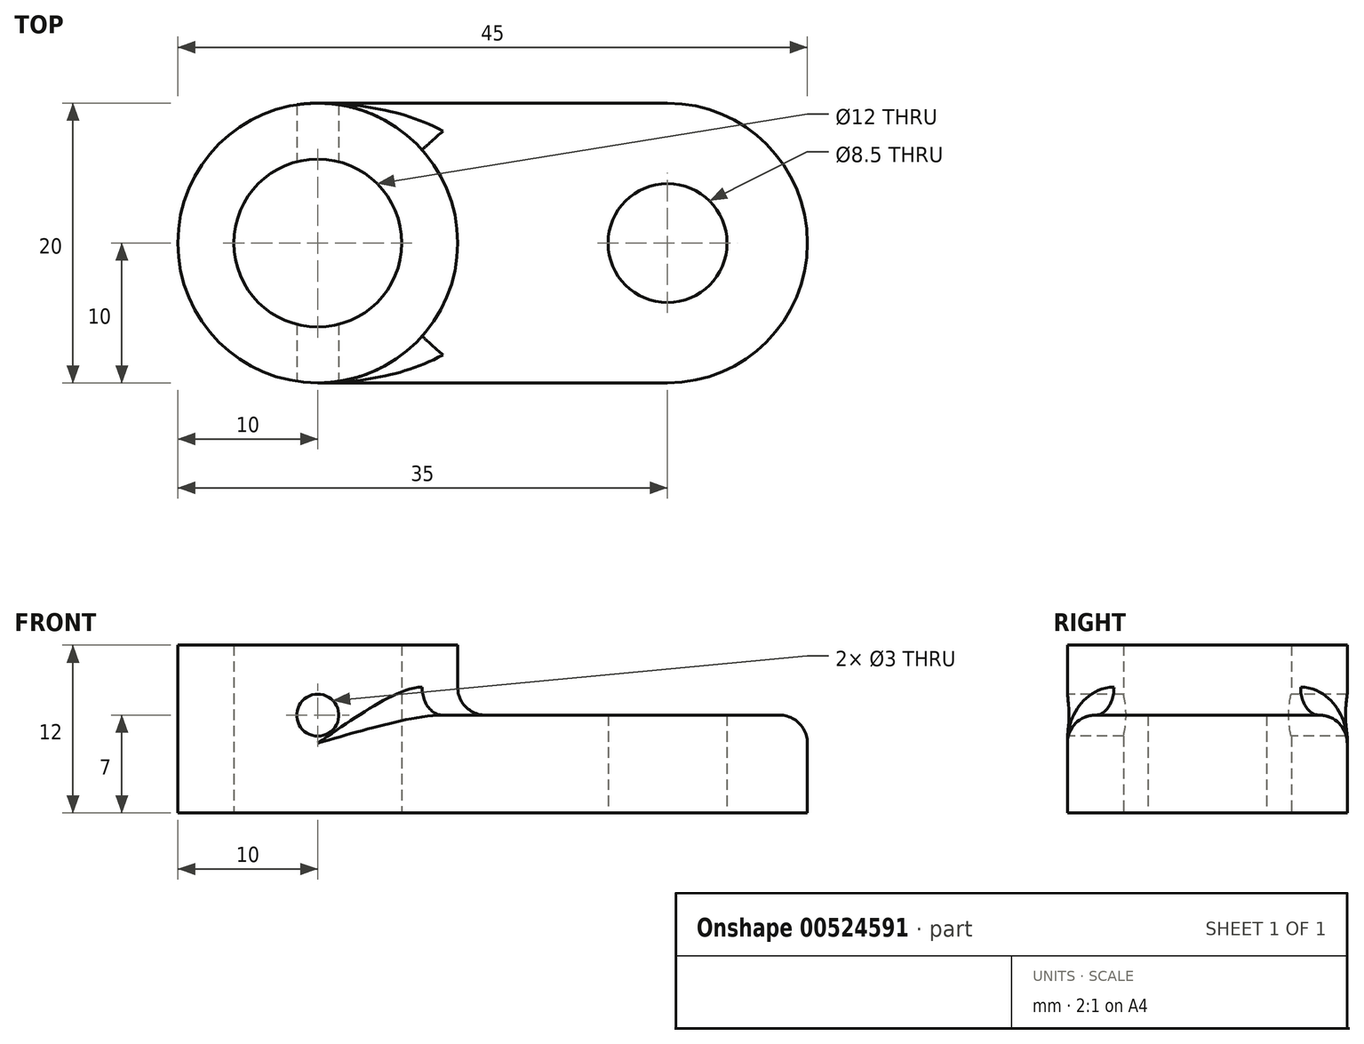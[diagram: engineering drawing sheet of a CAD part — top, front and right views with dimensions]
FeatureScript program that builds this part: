
annotation { "Feature Type Name" : "Feature", "Feature Type Description" : "" }
export const myFeature = defineFeature(function(context is Context, id is Id, definition is map)
    precondition{}
    {
        {
            var Q0;
            Q0=qCreatedBy(makeId("Top.planeOp"),FACE);
            var sketch = newSketch(context, id + "F0", { "sketchPlane" : qUnion([Q0])});
            skLineSegment(sketch, "E0", {"start": v(0, 0) * mm, "end": v(25, 0) * mm, "construction": true});
            skArc(sketch, "E1.0.startCap", {"start": v(0, -10) * mm, "mid": v(-10, 0) * mm, "end": v(0, 10) * mm});
            skArc(sketch, "E1.0.endCap", {"start": v(25, 10) * mm, "mid": v(35, 0) * mm, "end": v(25, -10) * mm});
            skLineSegment(sketch, "E1.0.left", {"start": v(0, 10) * mm, "end": v(25, 10) * mm});
            skLineSegment(sketch, "E1.0.right", {"start": v(0, -10) * mm, "end": v(25, -10) * mm});
            skCircle(sketch, "E2", {"center": v(0, 0) * mm, "radius": 6 * mm});
            skCircle(sketch, "E3", {"center": v(0, 0) * mm, "radius": 10 * mm});
            skCircle(sketch, "E4", {"center": v(25, 0) * mm, "radius": 4.25 * mm});
            skSolve(sketch);
        }
        {
            var Q0;
            Q0 = qSketchRegion(id + "F0", true);
            extrude(context, id + "F1", {"entities" : qUnion([Q0]), "depth" : 7 * mm, "offsetDistance" : 25 * mm});
        }
        {
            var Q0;
            Q0=makeQuery(id+"F0.imprint","IMPRINT",FACE,{"disambiguationData":[TD([[makeQuery(id+"F0.imprint","IMPRINT",EDGE,{"derivedFrom":sQuery(id+"F0.wireOp",EDGE,"E2")}),-1.0]])]});
            extrude(context, id + "F2", {"entities" : qUnion([Q0]), "operationType" : NewBodyOperationType.ADD, "depth" : 12 * mm, "offsetDistance" : 25 * mm});
        }
        {
            var Q0;
            Q0=qCreatedBy(makeId("Front.planeOp"),FACE);
            var sketch = newSketch(context, id + "F3", { "sketchPlane" : qUnion([Q0])});
            skLineSegment(sketch, "E5.0", {"start": v(0, 7) * mm, "end": v(25, 7) * mm});
            skCircle(sketch, "E6", {"center": v(0, 7) * mm, "radius": 1.5 * mm});
            skSolve(sketch);
        }
        {
            var Q0;
            {var subQ0=sQuery(id+"F0.wireOp",EDGE,"E3");Q0=makeQuery(id+"F2.boolean.opBoolean","INTERSECT",EDGE,{"derivedFrom":[makeQuery(id+"F1.opExtrude","CAP_FACE",FACE,{"disambiguationData":[OSD([sQuery(id+"F0.wireOp",EDGE,"E1.0.endCap"),sQuery(id+"F0.wireOp",EDGE,"E1.0.left"),sQuery(id+"F0.wireOp",EDGE,"E1.0.right"),sQuery(id+"F0.wireOp",EDGE,"E2"),subQ0,sQuery(id+"F0.wireOp",EDGE,"E4")])],"isStart":false}),makeQuery(id+"F2.opExtrude","SWEPT_FACE",FACE,{"disambiguationData":[OSD([subQ0])]})]});}
            var Q1;
            Q1=makeQuery(id+"F1.opExtrude","CAP_EDGE",EDGE,{"disambiguationData":[OSD([sQuery(id+"F0.wireOp",EDGE,"E1.0.right")])],"isStart":false});
            fillet(context, id + "F4", {"entities" : qUnion([Q0, Q1]), "radius" : 2 * mm, "tangentPropagation" : true, "allowEdgeOverflow" : false});
        }
        {
            var Q0;
            Q0 = qSketchRegion(id + "F3", true);
            extrude(context, id + "F5", {"entities" : qUnion([Q0]), "operationType" : NewBodyOperationType.REMOVE, "oppositeDirection" : true, "depth" : 25 * mm, "offsetDistance" : 25 * mm, "symmetric" : true});
        }
    });
